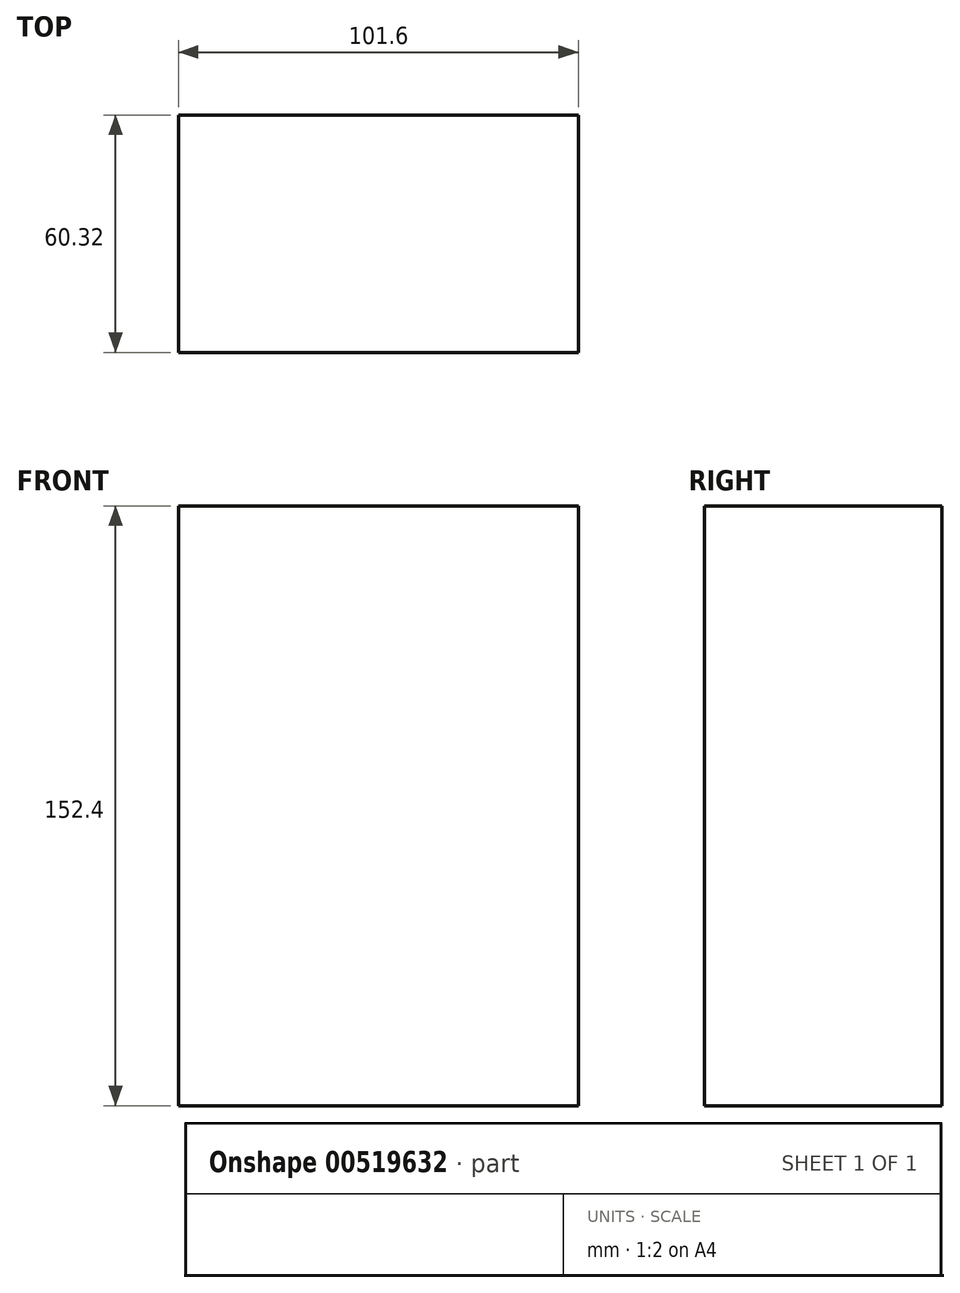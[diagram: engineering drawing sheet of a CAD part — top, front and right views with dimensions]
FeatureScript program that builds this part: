
annotation { "Feature Type Name" : "Feature", "Feature Type Description" : "" }
export const myFeature = defineFeature(function(context is Context, id is Id, definition is map)
    precondition{}
    {
        {
            var Q0;
            Q0=qCreatedBy(makeId("Front.planeOp"),FACE);
            var sketch = newSketch(context, id + "F0", { "sketchPlane" : qUnion([Q0])});
            skLineSegment(sketch, "E0.bottom", {"start": v(50.8, 76.2) * mm, "end": v(-50.8, 76.2) * mm});
            skLineSegment(sketch, "E0.top", {"start": v(50.8, -76.2) * mm, "end": v(-50.8, -76.2) * mm});
            skLineSegment(sketch, "E0.left", {"start": v(50.8, 76.2) * mm, "end": v(50.8, -76.2) * mm});
            skLineSegment(sketch, "E0.right", {"start": v(-50.8, 76.2) * mm, "end": v(-50.8, -76.2) * mm});
            skPoint(sketch, "E0.middle", {"position": v(0, 0) * mm});
            skSolve(sketch);
        }
        {
            var Q0;
            Q0=makeQuery(id+"F0.imprint","IMPRINT",FACE,{"disambiguationData":[TD([[makeQuery(id+"F0.imprint","IMPRINT",EDGE,{"derivedFrom":sQuery(id+"F0.wireOp",EDGE,"E0.bottom")}),1.0]])]});
            extrude(context, id + "F1", {"entities" : qUnion([Q0]), "endBound" : BoundingType.SYMMETRIC, "depth" : 60.32 * mm, "offsetDistance" : 25.4 * mm});
        }
    });
